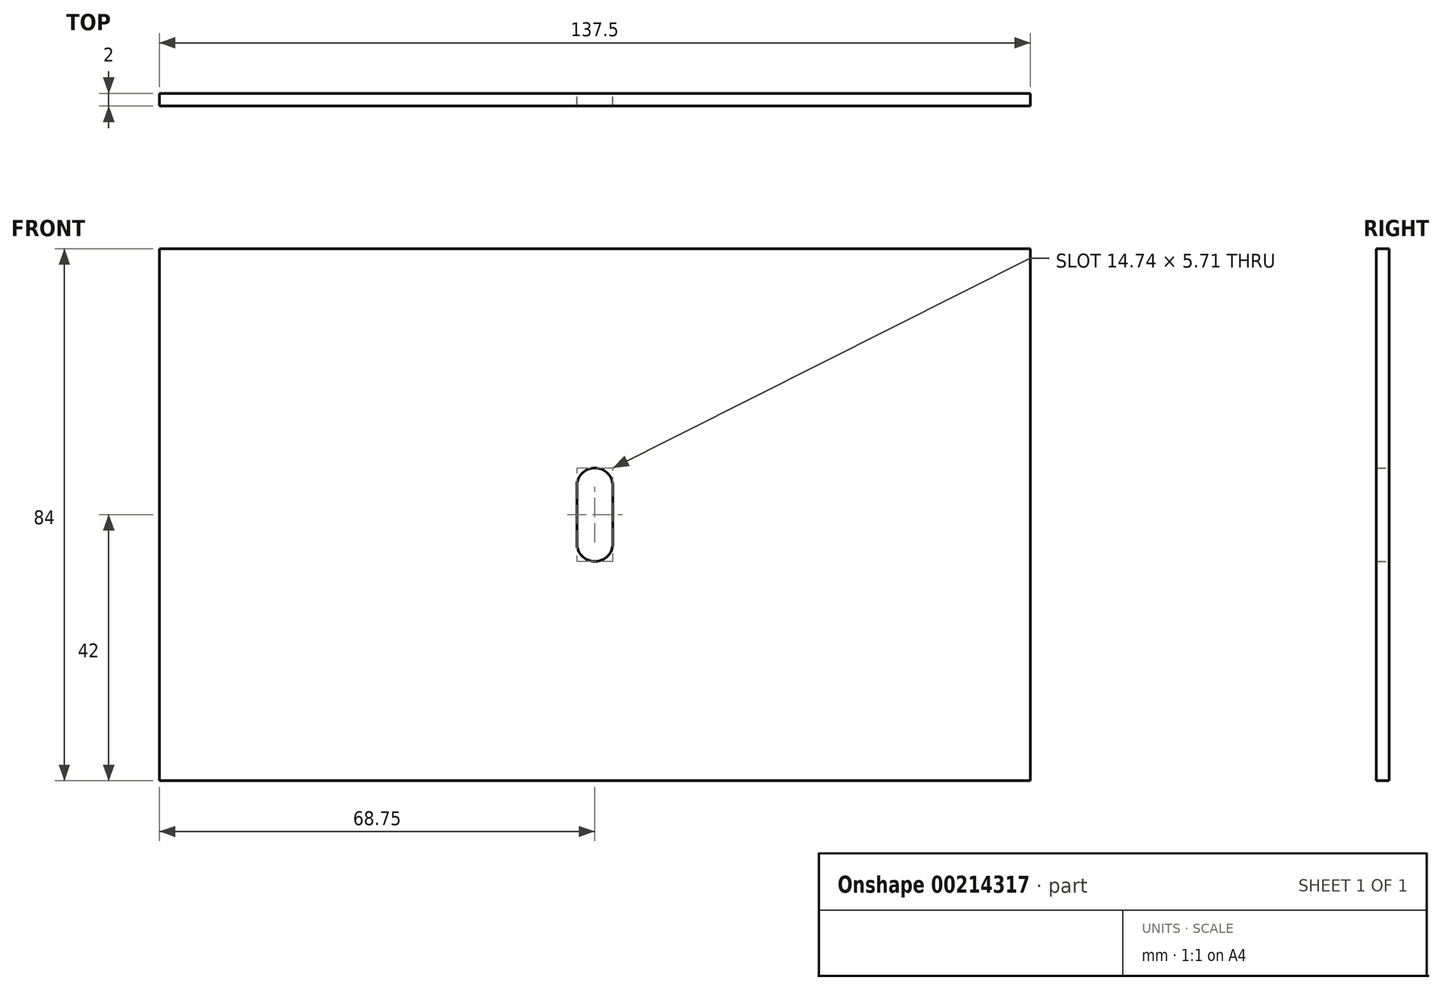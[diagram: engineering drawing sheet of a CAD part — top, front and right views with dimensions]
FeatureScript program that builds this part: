
annotation { "Feature Type Name" : "Feature", "Feature Type Description" : "" }
export const myFeature = defineFeature(function(context is Context, id is Id, definition is map)
    precondition{}
    {
        {
            var Q0;
            Q0=qCreatedBy(makeId("Front.planeOp"),FACE);
            var sketch = newSketch(context, id + "F0", { "sketchPlane" : qUnion([Q0])});
            skLineSegment(sketch, "E0.bottom", {"start": v(68.75, 42) * mm, "end": v(-68.75, 42) * mm});
            skLineSegment(sketch, "E0.top", {"start": v(68.75, -42) * mm, "end": v(-68.75, -42) * mm});
            skLineSegment(sketch, "E0.left", {"start": v(68.75, 42) * mm, "end": v(68.75, -42) * mm});
            skLineSegment(sketch, "E0.right", {"start": v(-68.75, 42) * mm, "end": v(-68.75, -42) * mm});
            skPoint(sketch, "E0.middle", {"position": v(0, 0) * mm});
            skLineSegment(sketch, "E1.left", {"start": v(2.85, 4.52) * mm, "end": v(2.85, -4.52) * mm});
            skLineSegment(sketch, "E1.right", {"start": v(-2.85, 4.52) * mm, "end": v(-2.85, -4.52) * mm});
            skArc(sketch, "E2", {"start": v(2.85, 4.52) * mm, "mid": v(0, 7.37) * mm, "end": v(-2.85, 4.52) * mm});
            skArc(sketch, "E3", {"start": v(-2.85, -4.52) * mm, "mid": v(0, -7.37) * mm, "end": v(2.85, -4.52) * mm});
            skSolve(sketch);
        }
        {
            var Q0;
            Q0=qSketchRegion(id+"F0",true);
            extrude(context, id + "F1", {"entities" : qUnion([Q0]), "depth" : 2 * mm});
        }
    });
